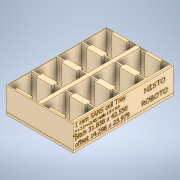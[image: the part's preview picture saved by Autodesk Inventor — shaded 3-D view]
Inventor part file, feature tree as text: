
AUTODESK INVENTOR PART (.ipt)
format: ipt  version: 2020 (Build 240168000, 168)  size: 2,768,896 bytes
history: native  units: in
note: dims shown in document units (in); Inventor stores cm internally (conversion verified against a paired STEP export)
features: extrude x3, sketch x3, fillet x1, emboss x1, pattern_linear x1
ambient origin geometry x8: Origin, YZ Plane, XZ Plane, XY Plane, X Axis, Y Axis, Z Axis, Center Point
bodies: Solid1 (feature_tree)
feature tree (9):
  extrude  "Extrusion1"  TaperAngle=45.0deg  [1 undecoded]
  extrude  "Extrusion2"  TaperAngle=225.0deg  [1 undecoded]
  extrude  "Extrusion3"  Depth=0.0394in TaperAngle=0.0deg
  fillet  "Fillet1"  Radius=0.0657in
  emboss  "Emboss2"
  pattern_linear  "Rectangular Pattern2"  Spacing1=0.1355in  [1 undecoded]
  sketch  "Sketch1"  dims[d3=0.0in d5=45.0deg]
  sketch  "Sketch2"  dims[d6=0.0079in d7=225.0deg]
  sketch  "Sketch5"  dims[d9=0.0in d48=0.0394in d49=0.0in d50=0.0657in d51=0.1355in d52=1.478in d53=0.957in d62=1.1811in d63=0.0in d64=1.5748in d66=1.2534in d67=0.7874in d69=1.6752in d70=0.35in d71=0.11in d72=0.35in d73=0.11in d74=0.35in d75=0.11in d76=0.35in d77=0.11in d65=0.0344in]
note: 3 required parameter values undecoded (feature->parameter linkage not recoverable at this tier; creation-order binding heuristic only, values carry confidence <= 0.55)
